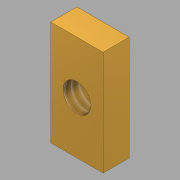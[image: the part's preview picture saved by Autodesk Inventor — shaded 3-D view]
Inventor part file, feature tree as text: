
AUTODESK INVENTOR PART (.ipt)
format: ipt  version: 2020 (Build 240168000, 168)  size: 95,232 bytes
history: native  units: in
note: dims shown in document units (in); Inventor stores cm internally (conversion verified against a paired STEP export)
features: sketch x2, other x1, extrude x1, hole x1
ambient origin geometry x8: Origin, YZ Plane, XZ Plane, XY Plane, X Axis, Y Axis, Z Axis, Center Point
bodies: Body1 (feature_tree)
feature tree (5):
  other  "Sólido1"
  extrude  "Extrusión1"  Depth=0.25in
  hole  "Agujero1"  [1 undecoded]
  sketch  "Boceto1"  dims[d0=0.125in d1=0.25in]
  sketch  "Boceto2"  dims[d2=0.0625in d3=0.0in d4=0.25in d5=0.125in d6=0.0625in d7=0.125in d8=0.0667in d9=0.172in d10=0.26in d11=0.25in d12=0.5635in d13=0.261in d14=0.8108in]
note: 1 required parameter value undecoded (feature->parameter linkage not recoverable at this tier; creation-order binding heuristic only, values carry confidence <= 0.55)
